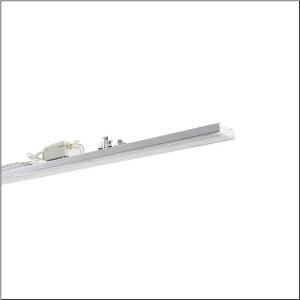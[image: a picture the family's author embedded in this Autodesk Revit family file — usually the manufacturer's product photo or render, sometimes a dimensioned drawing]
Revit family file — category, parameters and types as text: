
# Revit family: licross_r__21_recessed_mo_52te18cn49xg_07a5
name_source: partatom
category: Lighting Fixtures
units: mm (PartAtom-declared; Revit-internal decimal feet)

## family parameters
Cut with Voids When Loaded = No
Host = Face
Light Source = No
Part Type = Normal
Room Calculation Point = No
Round Connector Dimension = Use Diameter
Shared = No

## types (1)
- --- (1 x LED, 9000 lm, 49.9 W, 4000K)
    Apparent Load = 50 VA
    CIE Flux Codes = 79 95 99 100 100
    Color Rendering = 80
    Color Temperature = 4000K
    Default Elevation = 1800 mm
    Description = Licross® 21 Recessed MO, luminaire insert, of sheet steel, galvanised, coil coated, white, length: 1.500mm, width: 66mm, height: 67mm, LED rated luminous flux: 9.000lm, light colour: 840, control gear: ON/OFF Multilumen, CLOi, control gear: ECG Multilumen, with plug, 3-pole, with phase selection, mains connection: 220..240V, AC, 50/60Hz, start of lifetime: 50W, end of service life: 61W, halogen-free wiring, primary light control with lens, of plastic, primary optical cover: cover, of PMMA, light emission: direct distribution, primary light characteristic: symmetric, protection rating (complete): IP54, insulation class (complete): insulation class I (protective earthing), certification: CE, ENEC, VDE, UKCA, protection symbol: D if used in an environment with non-conductive dust loads with corresponding accessories, impact resistance: IK06, permissible ambient temperature for indoor applications: -35..+40°C, corresponds to IFS (International Featured Standards) requirements for safety and quality in the food industry, reducing of maximum allowable ambient temperature of 5°C with ceiling mounting, LABS conformity tested according to VDMA 24364:2018-05, packaging unit: 1 piece
    Height = 58 mm
    Lamp = 1 x LED
    Lamp Light Flux = 9000 lm
    Lamp Power = 49.9 W
    Lamp count = 1
    Length = 1500 mm
    Luminous efficacy = 180 lm/W
    Manufacturer = Siteco
    ModVariant = No
    Model = 52TE18CN49XG
    Mounting Place = Ceiling
    Mounting Type = Pendant
    Number of Poles = 1
    OnlyDefault = Yes
    Power Factor = 1
    Product Name = Licross® 21 Recessed MO
    Product group = luminaire insert
    ProductGroupID = 901
    Protection Class = Protection class I
    Protection Degree = IP 54
    RLX_Detail_Level = 1
    RLX_Emergency_Light_Flux = 0 lm
    RLX_Emergency_Type = 0
    RLX_Emergency_Type_DB = No
    RlxData = <blob elided: 22329 chars, md5=83715f96>
    Socket = socket
    Standby Power = 0 W
    System Light Flux = 9000 lm
    System Power = 50 W
    Type Comments = factory setting: luminous flux: 100 % | (A | C | E) | 116 mA
    Type Image = l_1296930.jpg
    URL = http://relux.com
    VarID = @adj_040145
    Voltage = 0 V
    Weight = 0.00 kg
    Width = 66 mm

## geometry (parser evidence)
native form markers: Blend x4, Sweep x11
no freeform markers — native parametric forms only
